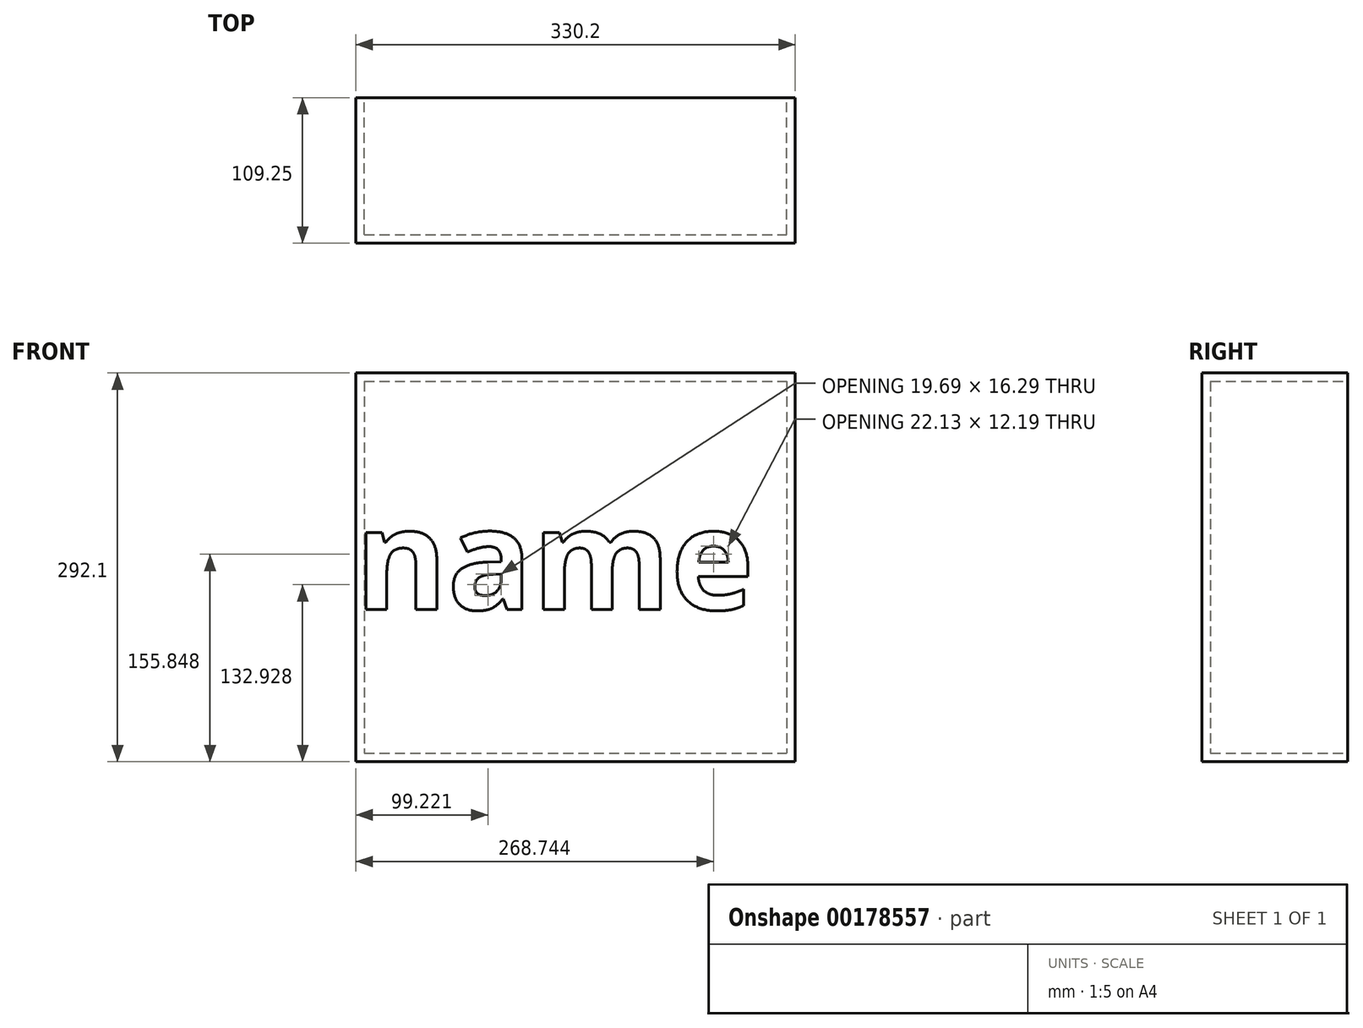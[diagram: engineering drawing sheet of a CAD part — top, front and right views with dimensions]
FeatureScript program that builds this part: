
annotation { "Feature Type Name" : "Feature", "Feature Type Description" : "" }
export const myFeature = defineFeature(function(context is Context, id is Id, definition is map)
    precondition{}
    {
        {
            var Q0;
            Q0=qCreatedBy(makeId("Front.planeOp"),FACE);
            var sketch = newSketch(context, id + "F0", { "sketchPlane" : qUnion([Q0])});
            skLineSegment(sketch, "E0.bottom", {"start": v(-179.35, 211.82) * mm, "end": v(150.85, 211.82) * mm});
            skLineSegment(sketch, "E0.top", {"start": v(-179.35, -80.28) * mm, "end": v(150.85, -80.28) * mm});
            skLineSegment(sketch, "E0.left", {"start": v(-179.35, 211.82) * mm, "end": v(-179.35, -80.28) * mm});
            skLineSegment(sketch, "E0.right", {"start": v(150.85, 211.82) * mm, "end": v(150.85, -80.28) * mm});
            skSolve(sketch);
        }
        {
            var Q0;
            Q0=qSketchRegion(id+"F0",true);
            extrude(context, id + "F1", {"entities" : qUnion([Q0]), "depth" : 109.22 * mm});
        }
        {
            var Q0;
            Q0=makeQuery(id+"F1.opExtrude","CAP_FACE",FACE,{"disambiguationData":[OSD([sQuery(id+"F0.wireOp",EDGE,"E0.bottom"),sQuery(id+"F0.wireOp",EDGE,"E0.top"),sQuery(id+"F0.wireOp",EDGE,"E0.left"),sQuery(id+"F0.wireOp",EDGE,"E0.right")])],"isStart":true});
            shell(context, id + "F2", {"entities" : qUnion([Q0]), "thickness" : 6.35 * mm});
        }
        {
            var Q0;
            Q0=makeQuery(id+"F1.opExtrude","CAP_FACE",FACE,{"disambiguationData":[OSD([sQuery(id+"F0.wireOp",EDGE,"E0.bottom"),sQuery(id+"F0.wireOp",EDGE,"E0.top"),sQuery(id+"F0.wireOp",EDGE,"E0.left"),sQuery(id+"F0.wireOp",EDGE,"E0.right")])],"isStart":false});
            cPlane(context, id + "F3", {"entities" : qUnion([Q0]), "cplaneType" : CPlaneType.OFFSET, "offset" : 0 * mm, "width" : 152.4 * mm, "height" : 152.4 * mm});
        }
        {
            var Q0;
            Q0=qCreatedBy(id+"F3.planeOp",FACE);
            var sketch = newSketch(context, id + "F4", { "sketchPlane" : qUnion([Q0])});
            skText(sketch, "E1", { "text": "name", "fontName": "OpenSans-Bold.ttf"});
            const initialGuessF4  = {"E1": [-0.18015, 0.03402, 1, 0, 0.0762]};
            skSetInitialGuess(sketch, initialGuessF4);
            skSolve(sketch);
        }
        {
            var Q0;
            Q0=qSketchRegion(id+"F4",true);
            extrude(context, id + "F5", {"entities" : qUnion([Q0]), "depth" : 0.03 * mm});
        }
    });
